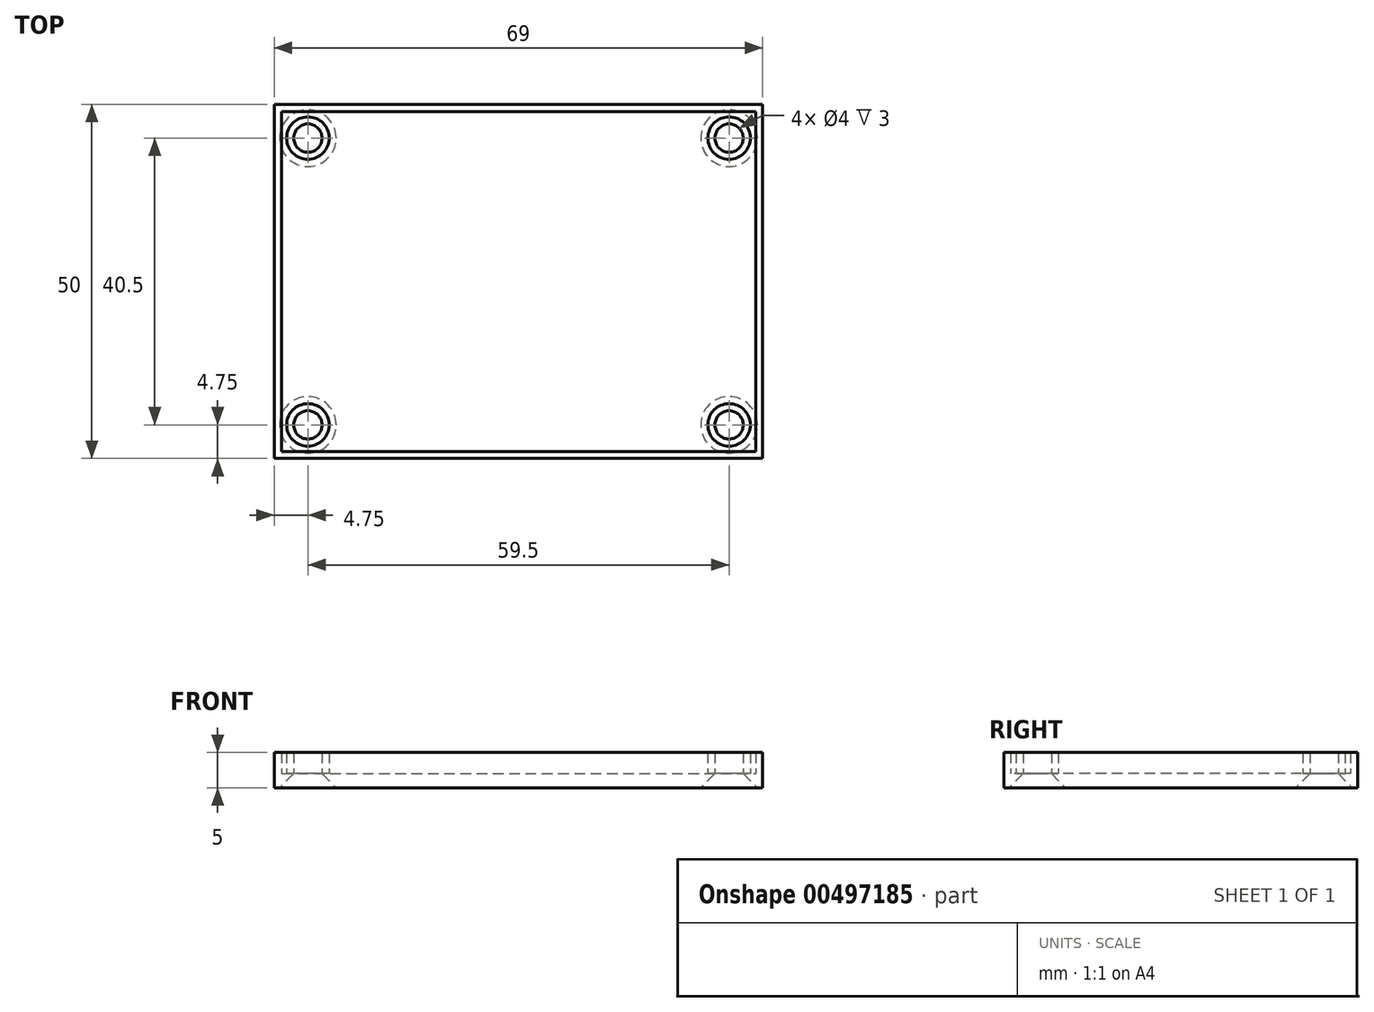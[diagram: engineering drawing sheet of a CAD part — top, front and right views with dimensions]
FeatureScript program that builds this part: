
annotation { "Feature Type Name" : "Feature", "Feature Type Description" : "" }
export const myFeature = defineFeature(function(context is Context, id is Id, definition is map)
    precondition{}
    {
        {
            var Q0;
            Q0=qCreatedBy(makeId("Top.planeOp"),FACE);
            var sketch = newSketch(context, id + "F0", { "sketchPlane" : qUnion([Q0])});
            skLineSegment(sketch, "E0.bottom", {"start": v(-33.5, 24) * mm, "end": v(33.5, 24) * mm});
            skLineSegment(sketch, "E0.top", {"start": v(-33.5, -24) * mm, "end": v(33.5, -24) * mm});
            skLineSegment(sketch, "E0.left", {"start": v(-33.5, 24) * mm, "end": v(-33.5, -24) * mm});
            skLineSegment(sketch, "E0.right", {"start": v(33.5, 24) * mm, "end": v(33.5, -24) * mm});
            skPoint(sketch, "E0.middle", {"position": v(0, 0) * mm});
            skLineSegment(sketch, "E1.bottom", {"start": v(-34.5, 25) * mm, "end": v(34.5, 25) * mm});
            skLineSegment(sketch, "E1.top", {"start": v(-34.5, -25) * mm, "end": v(34.5, -25) * mm});
            skLineSegment(sketch, "E1.left", {"start": v(-34.5, 25) * mm, "end": v(-34.5, -25) * mm});
            skLineSegment(sketch, "E1.right", {"start": v(34.5, 25) * mm, "end": v(34.5, -25) * mm});
            skPoint(sketch, "E2", {"position": v(-29.75, 20.25) * mm});
            skPoint(sketch, "E3", {"position": v(29.75, -20.25) * mm});
            skPoint(sketch, "E4", {"position": v(-29.75, -20.25) * mm});
            skCircle(sketch, "E5", {"center": v(-29.75, 20.25) * mm, "radius": 2 * mm});
            skCircle(sketch, "E6", {"center": v(-29.75, -20.25) * mm, "radius": 2 * mm});
            skCircle(sketch, "E7", {"center": v(29.75, -20.25) * mm, "radius": 2 * mm});
            skPoint(sketch, "E8", {"position": v(29.75, 20.25) * mm});
            skCircle(sketch, "E9", {"center": v(29.75, 20.25) * mm, "radius": 2 * mm});
            skCircle(sketch, "E10", {"center": v(-29.75, 20.25) * mm, "radius": 3 * mm});
            skCircle(sketch, "E11", {"center": v(29.75, 20.25) * mm, "radius": 3 * mm});
            skCircle(sketch, "E12", {"center": v(29.75, -20.25) * mm, "radius": 3 * mm});
            skCircle(sketch, "E13", {"center": v(-29.75, -20.25) * mm, "radius": 3 * mm});
            skSolve(sketch);
        }
        {
            var Q0;
            Q0=makeQuery(id+"F0.imprint","IMPRINT",FACE,{"disambiguationData":[TD([[makeQuery(id+"F0.imprint","IMPRINT",EDGE,{"derivedFrom":sQuery(id+"F0.wireOp",EDGE,"E0.bottom")}),-1.0]])]});
            extrude(context, id + "F1", {"entities" : qUnion([Q0]), "depth" : 2 * mm, "offsetDistance" : 25 * mm});
        }
        {
            var Q0;
            Q0=makeQuery(id+"F0.imprint","IMPRINT",FACE,{"disambiguationData":[TD([[makeQuery(id+"F0.imprint","IMPRINT",EDGE,{"derivedFrom":sQuery(id+"F0.wireOp",EDGE,"E5")}),-1.0]])]});
            var Q1;
            Q1=makeQuery(id+"F0.imprint","IMPRINT",FACE,{"disambiguationData":[TD([[makeQuery(id+"F0.imprint","IMPRINT",EDGE,{"derivedFrom":sQuery(id+"F0.wireOp",EDGE,"E9")}),-1.0]])]});
            var Q2;
            Q2=makeQuery(id+"F0.imprint","IMPRINT",FACE,{"disambiguationData":[TD([[makeQuery(id+"F0.imprint","IMPRINT",EDGE,{"derivedFrom":sQuery(id+"F0.wireOp",EDGE,"E7")}),-1.0]])]});
            var Q3;
            Q3=makeQuery(id+"F0.imprint","IMPRINT",FACE,{"disambiguationData":[TD([[makeQuery(id+"F0.imprint","IMPRINT",EDGE,{"derivedFrom":sQuery(id+"F0.wireOp",EDGE,"E6")}),-1.0]])]});
            extrude(context, id + "F2", {"entities" : qUnion([Q0, Q1, Q2, Q3]), "operationType" : NewBodyOperationType.ADD, "depth" : 5 * mm, "offsetDistance" : 25 * mm});
        }
        {
            var Q0;
            Q0=makeQuery(id+"F0.imprint","IMPRINT",FACE,{"disambiguationData":[TD([[makeQuery(id+"F0.imprint","IMPRINT",EDGE,{"derivedFrom":sQuery(id+"F0.wireOp",EDGE,"E0.bottom")}),1.0]])]});
            extrude(context, id + "F3", {"entities" : qUnion([Q0]), "operationType" : NewBodyOperationType.ADD, "depth" : 5 * mm, "offsetDistance" : 25 * mm});
        }
        {
            var Q0;
            Q0=makeQuery(id+"F2.opExtrude","CAP_EDGE",EDGE,{"disambiguationData":[OSD([sQuery(id+"F0.wireOp",EDGE,"E7")])],"isStart":true});
            var Q1;
            Q1=makeQuery(id+"F2.opExtrude","CAP_EDGE",EDGE,{"disambiguationData":[OSD([sQuery(id+"F0.wireOp",EDGE,"E9")])],"isStart":true});
            var Q2;
            Q2=makeQuery(id+"F2.opExtrude","CAP_EDGE",EDGE,{"disambiguationData":[OSD([sQuery(id+"F0.wireOp",EDGE,"E5")])],"isStart":true});
            var Q3;
            Q3=makeQuery(id+"F2.opExtrude","CAP_EDGE",EDGE,{"disambiguationData":[OSD([sQuery(id+"F0.wireOp",EDGE,"E6")])],"isStart":true});
            chamfer(context, id + "F4", {"entities" : qUnion([Q0, Q1, Q2, Q3]), "width" : 2 * mm, "tangentPropagation" : true});
        }
    });
